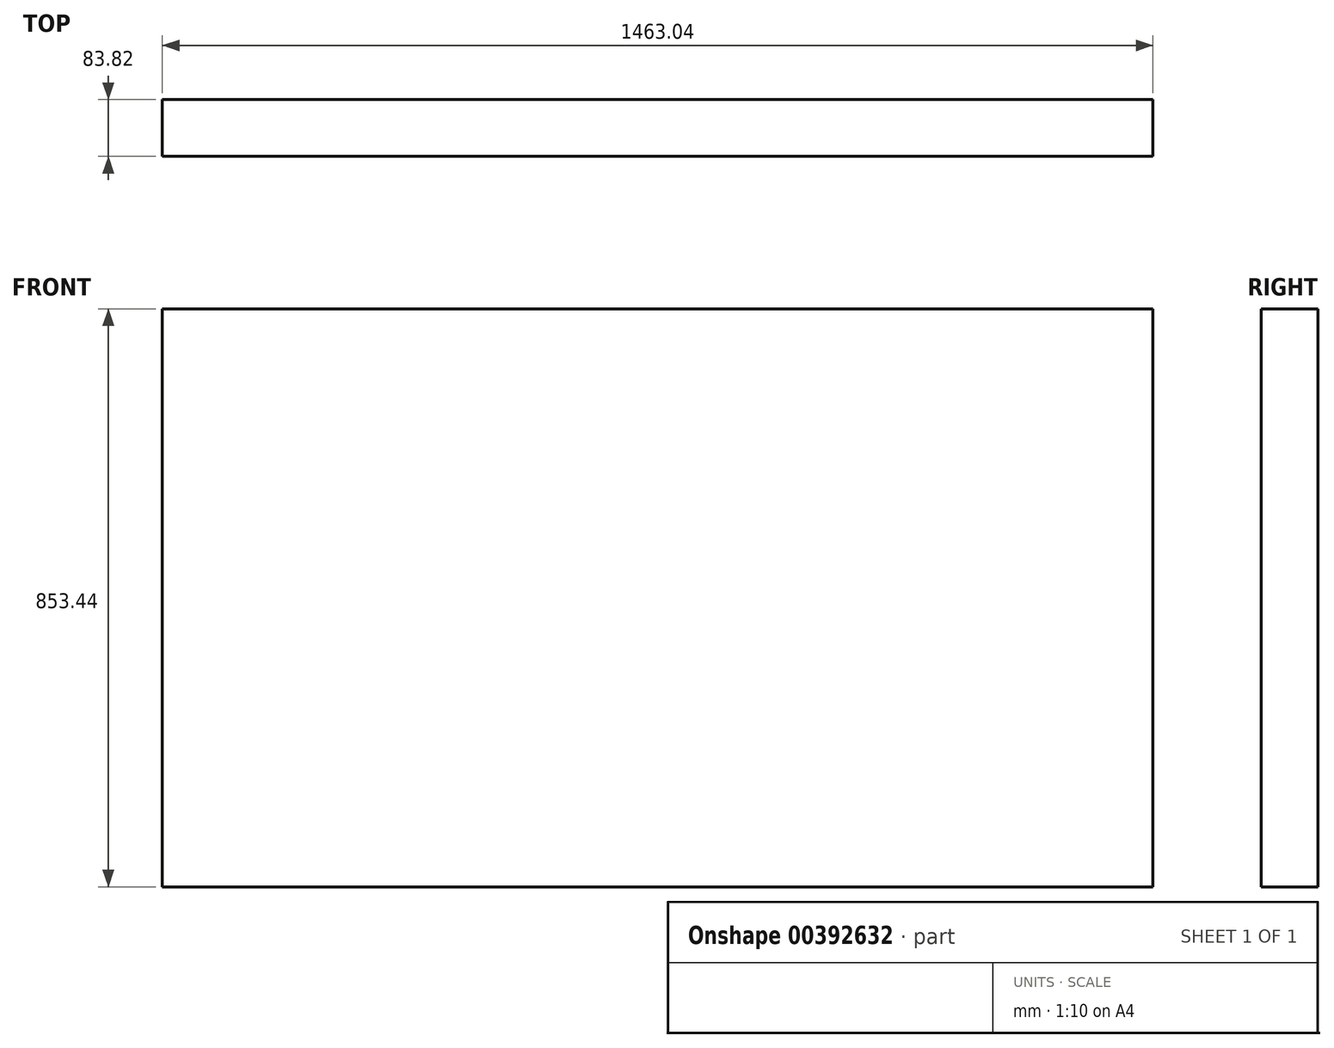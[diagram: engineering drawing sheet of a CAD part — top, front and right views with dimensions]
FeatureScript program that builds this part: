
annotation { "Feature Type Name" : "Feature", "Feature Type Description" : "" }
export const myFeature = defineFeature(function(context is Context, id is Id, definition is map)
    precondition{}
    {
        {
            var Q0;
            Q0=qCreatedBy(makeId("Front.planeOp"),FACE);
            var sketch = newSketch(context, id + "F0", { "sketchPlane" : qUnion([Q0])});
            skLineSegment(sketch, "E0.bottom", {"start": v(731.52, -426.72) * mm, "end": v(-731.52, -426.72) * mm});
            skLineSegment(sketch, "E0.top", {"start": v(731.52, 426.72) * mm, "end": v(-731.52, 426.72) * mm});
            skLineSegment(sketch, "E0.left", {"start": v(731.52, -426.72) * mm, "end": v(731.52, 426.72) * mm});
            skLineSegment(sketch, "E0.right", {"start": v(-731.52, -426.72) * mm, "end": v(-731.52, 426.72) * mm});
            skPoint(sketch, "E0.middle", {"position": v(0, 0) * mm});
            skSolve(sketch);
        }
        {
            var Q0;
            Q0=makeQuery(id+"F0.imprint","IMPRINT",FACE,{"disambiguationData":[TD([[makeQuery(id+"F0.imprint","IMPRINT",EDGE,{"derivedFrom":sQuery(id+"F0.wireOp",EDGE,"E0.bottom")}),-1.0]])]});
            extrude(context, id + "F1", {"entities" : qUnion([Q0]), "oppositeDirection" : true, "depth" : 83.82 * mm});
        }
    });
